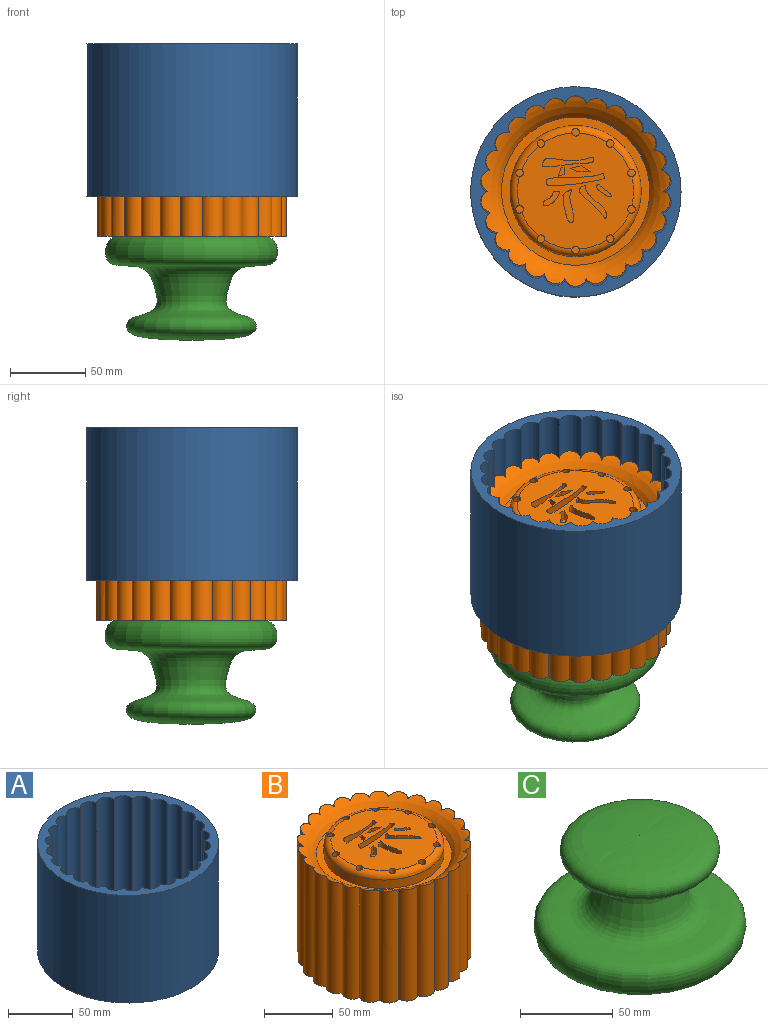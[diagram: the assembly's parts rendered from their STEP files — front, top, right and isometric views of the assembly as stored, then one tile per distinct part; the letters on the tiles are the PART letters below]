
ASSEMBLY  parts=3 mates=2
PART A: 30 faces, bbox 139.7x139.7x101.6 mm
  f0: plane 139.7x139.7mm, normal (0,0,-1), area 15327.9mm2, adj f1
  f1: cylinder r=69.85mm len=139.7mm, axis (0,0,-1), area 44590.3mm2, adj f0,f2
  f2: plane 139.7x139.7mm, normal (0,0,1), area 3055.9mm2, adj f1,f3,f4,f5,f6,f7,f8,f9
  f3: cylinder r=7.62mm len=99.06mm, axis (0,0,1), area 1835.1mm2, adj f2,f4,f11,f29
  f4: cylinder r=7.62mm len=99.06mm, axis (0,0,1), area 1835.1mm2, adj f2,f3,f28,f29
  f5: cylinder r=7.62mm len=99.06mm, axis (0,0,1), area 1835.1mm2, adj f2,f7,f10,f29
  f6: cylinder r=7.62mm len=99.06mm, axis (0,0,1), area 1835.1mm2, adj f2,f8,f9,f29
  f7: cylinder r=7.62mm len=99.06mm, axis (0,0,1), area 1835.1mm2, adj f2,f5,f8,f29
  f8: cylinder r=7.62mm len=99.06mm, axis (0,0,1), area 1835.1mm2, adj f2,f6,f7,f29
  f9: cylinder r=7.62mm len=99.06mm, axis (0,0,1), area 1835.1mm2, adj f2,f6,f12,f29
  f10: cylinder r=7.62mm len=99.06mm, axis (0,0,1), area 1835.1mm2, adj f2,f5,f11,f29
  f11: cylinder r=7.62mm len=99.06mm, axis (0,0,1), area 1835.1mm2, adj f2,f3,f10,f29
  f12: cylinder r=7.62mm len=99.06mm, axis (0,0,1), area 1835.1mm2, adj f2,f9,f13,f29
  f13: cylinder r=7.62mm len=99.06mm, axis (0,0,1), area 1835.1mm2, adj f2,f12,f14,f29
  f14: cylinder r=7.62mm len=99.06mm, axis (0,0,1), area 1835.1mm2, adj f2,f13,f15,f29
  f15: cylinder r=7.62mm len=99.06mm, axis (0,0,1), area 1835.1mm2, adj f2,f14,f16,f29
  f16: cylinder r=7.62mm len=99.06mm, axis (0,0,1), area 1835.1mm2, adj f2,f15,f17,f29
  f17: cylinder r=7.62mm len=99.06mm, axis (0,0,1), area 1835.1mm2, adj f2,f16,f18,f29
  f18: cylinder r=7.62mm len=99.06mm, axis (0,0,1), area 1835.1mm2, adj f2,f17,f19,f29
  f19: cylinder r=7.62mm len=99.06mm, axis (0,0,1), area 1835.1mm2, adj f2,f18,f20,f29
  f20: cylinder r=7.62mm len=99.06mm, axis (0,0,1), area 1835.1mm2, adj f2,f19,f21,f29
  f21: cylinder r=7.62mm len=99.06mm, axis (0,0,1), area 1835.1mm2, adj f2,f20,f22,f29
  f22: cylinder r=7.62mm len=99.06mm, axis (0,0,1), area 1835.1mm2, adj f2,f21,f23,f29
  f23: cylinder r=7.62mm len=99.06mm, axis (0,0,1), area 1835.1mm2, adj f2,f22,f24,f29
  f24: cylinder r=7.62mm len=99.06mm, axis (0,0,1), area 1835.1mm2, adj f2,f23,f25,f29
  f25: cylinder r=7.62mm len=99.06mm, axis (0,0,1), area 1835.1mm2, adj f2,f24,f27,f29
  f26: cylinder r=7.62mm len=99.06mm, axis (0,0,1), area 1835.1mm2, adj f2,f27,f28,f29
  f27: cylinder r=7.62mm len=99.06mm, axis (0,0,1), area 1835.1mm2, adj f2,f25,f26,f29
  f28: cylinder r=7.62mm len=99.06mm, axis (0,0,1), area 1835.1mm2, adj f2,f4,f26,f29
  f29: plane 127.62x126.8mm, normal (0,0,1), area 12272mm2, adj f3,f4,f5,f6,f7,f8,f9,f10
PART B: 77 faces, bbox 153.7x153.7x100.6 mm
  f0: plane 77.12x76.96mm, normal (0,0,1), area 4000.1mm2, adj f1,f32,f34,f36,f38,f40,f42,f44
  f1: torus R=38.56mm, axis (0,0,1), area 1934.2mm2, adj f0,f31,f32,f34,f36,f38,f40,f42
  f2: cylinder r=7.54mm len=99.33mm, axis (0,0,-1), area 1810.4mm2, adj f3,f4,f5,f30
  f3: plane 126.34x125.53mm, normal (0,0,-1), area 12027.8mm2, adj f2,f4,f5,f6,f7,f8,f9,f10
  f4: cylinder r=7.54mm len=99.33mm, axis (0,0,-1), area 1810.4mm2, adj f2,f3,f6,f30
  f5: cylinder r=7.54mm len=99.33mm, axis (0,0,-1), area 1810.4mm2, adj f2,f3,f12,f30
  f6: cylinder r=7.54mm len=99.33mm, axis (0,0,-1), area 1810.4mm2, adj f3,f4,f7,f30
  f7: cylinder r=7.54mm len=99.33mm, axis (0,0,-1), area 1810.4mm2, adj f3,f6,f8,f30
  f8: cylinder r=7.54mm len=99.33mm, axis (0,0,-1), area 1810.4mm2, adj f3,f7,f9,f30
  f9: cylinder r=7.54mm len=99.33mm, axis (0,0,-1), area 1810.4mm2, adj f3,f8,f10,f30
  f10: cylinder r=7.54mm len=99.33mm, axis (0,0,-1), area 1810.4mm2, adj f3,f9,f11,f30
  f11: cylinder r=7.54mm len=99.33mm, axis (0,0,-1), area 1810.4mm2, adj f3,f10,f28,f30
  f12: cylinder r=7.54mm len=99.33mm, axis (0,0,-1), area 1810.4mm2, adj f3,f5,f13,f30
  f13: cylinder r=7.54mm len=99.33mm, axis (0,0,-1), area 1810.4mm2, adj f3,f12,f14,f30
  f14: cylinder r=7.54mm len=99.33mm, axis (0,0,-1), area 1810.4mm2, adj f3,f13,f15,f30
  f15: cylinder r=7.54mm len=99.33mm, axis (0,0,-1), area 1810.4mm2, adj f3,f14,f16,f30
  f16: cylinder r=7.54mm len=99.33mm, axis (0,0,-1), area 1810.4mm2, adj f3,f15,f17,f30
  f17: cylinder r=7.54mm len=99.33mm, axis (0,0,-1), area 1810.4mm2, adj f3,f16,f18,f30
  f18: cylinder r=7.54mm len=99.33mm, axis (0,0,-1), area 1810.4mm2, adj f3,f17,f19,f30
  f19: cylinder r=7.54mm len=99.33mm, axis (0,0,-1), area 1810.4mm2, adj f3,f18,f20,f30
  f20: cylinder r=7.54mm len=99.33mm, axis (0,0,-1), area 1810.4mm2, adj f3,f19,f21,f30
  f21: cylinder r=7.54mm len=99.33mm, axis (0,0,-1), area 1810.4mm2, adj f3,f20,f22,f30
  f22: cylinder r=7.54mm len=99.33mm, axis (0,0,-1), area 1810.4mm2, adj f3,f21,f23,f30
  f23: cylinder r=7.54mm len=99.33mm, axis (0,0,-1), area 1810.4mm2, adj f3,f22,f24,f30
  f24: cylinder r=7.54mm len=99.33mm, axis (0,0,-1), area 1810.4mm2, adj f3,f23,f25,f30
  f25: cylinder r=7.54mm len=99.33mm, axis (0,0,-1), area 1810.4mm2, adj f3,f24,f26,f30
  f26: cylinder r=7.54mm len=99.33mm, axis (0,0,-1), area 1810.4mm2, adj f3,f25,f27,f30
  f27: cylinder r=7.54mm len=99.33mm, axis (0,0,-1), area 1810.4mm2, adj f3,f26,f28,f30
  f28: cylinder r=7.54mm len=99.33mm, axis (0,0,-1), area 1810.4mm2, adj f3,f11,f27,f30
  f29: plane 98.49x98.49mm, normal (0,0,1), area 1648.6mm2, adj f30,f31
  f30: torus R=71.02mm, axis (0,0,1), area 5854.1mm2, adj f2,f4,f5,f6,f7,f8,f9,f10
  f31: cylinder r=43.59mm len=87.18mm, axis (0,0,-1), area 2066.2mm2, adj f1,f29
  f32: cylinder r=2.55mm len=7.54mm, axis (0,0,1), area 116.3mm2, adj f0,f1,f33
  f33: plane 5.11x5.11mm, normal (0,0,1), area 20.5mm2, adj f32
  f34: cylinder r=2.55mm len=7.54mm, axis (0,0,1), area 116.3mm2, adj f0,f1,f35
  f35: plane 5.11x5.11mm, normal (0,0,1), area 20.5mm2, adj f34
  f36: cylinder r=2.55mm len=7.54mm, axis (0,0,1), area 116.3mm2, adj f0,f1,f37
  f37: plane 5.11x5.11mm, normal (0,0,1), area 20.5mm2, adj f36
  f38: cylinder r=2.55mm len=7.54mm, axis (0,0,1), area 116.3mm2, adj f0,f1,f39
  f39: plane 5.11x5.11mm, normal (0,0,1), area 20.5mm2, adj f38
  f40: cylinder r=2.55mm len=7.54mm, axis (0,0,1), area 116.3mm2, adj f0,f1,f41
  f41: plane 5.11x5.11mm, normal (0,0,1), area 20.5mm2, adj f40
  f42: cylinder r=2.55mm len=7.54mm, axis (0,0,1), area 116.3mm2, adj f0,f1,f43
  f43: plane 5.11x5.11mm, normal (0,0,1), area 20.5mm2, adj f42
  f44: cylinder r=2.55mm len=7.54mm, axis (0,0,1), area 116.3mm2, adj f0,f1,f45
  f45: plane 5.11x5.11mm, normal (0,0,1), area 20.5mm2, adj f44
  f46: cylinder r=2.55mm len=7.54mm, axis (0,0,1), area 116.3mm2, adj f0,f1,f47
  f47: plane 5.11x5.11mm, normal (0,0,1), area 20.5mm2, adj f46
  f48: cylinder r=2.55mm len=7.54mm, axis (0,0,1), area 116.3mm2, adj f0,f1,f49
  f49: plane 5.11x5.11mm, normal (0,0,1), area 20.5mm2, adj f48
  f50: cylinder r=2.55mm len=7.54mm, axis (0,0,1), area 116.3mm2, adj f0,f1,f51
  f51: plane 5.11x5.11mm, normal (0,0,1), area 20.5mm2, adj f50
  f52: extruded ~32.28x7.54mm, area 274.2mm2, adj f0,f53,f54
  f53: extruded ~34.1x7.54mm, area 290.2mm2, adj f0,f52,f54
  f54: plane 34.34x6.81mm, normal (0,0,1), area 118.8mm2, adj f52,f53
  f55: plane 7.54x2.26mm, normal (0.23,-0.97,0), area 17.5mm2, adj f0,f56,f58,f59
  f56: plane 7.54x5.33mm, normal (0.96,-0.29,0), area 42mm2, adj f0,f55,f57,f59
  f57: plane 7.54x3.84mm, normal (-0.23,0.97,0), area 29.8mm2, adj f0,f56,f58,f59
  f58: plane 7.54x4.96mm, normal (-1,0,0), area 37.4mm2, adj f0,f55,f57,f59
  f59: plane 5.86x3.84mm, normal (0,0,1), area 15.1mm2, adj f55,f56,f57,f58
  f60: plane 7.54x2.88mm, normal (0.63,-0.78,0), area 28mm2, adj f0,f61,f62
  f61: extruded ~21.76x7.54mm, area 345.1mm2, adj f0,f60,f62
  f62: plane 23.1x7.83mm, normal (0,0,1), area 94.2mm2, adj f60,f61
  f63: plane 7.54x4.08mm, normal (0,-1,0), area 30.8mm2, adj f0,f64,f65
  f64: extruded ~10.9x9.85mm, area 212.8mm2, adj f0,f63,f65
  f65: plane 11.17x10.13mm, normal (0,0,1), area 47.2mm2, adj f63,f64
  f66: plane 7.54x6.97mm, normal (0.23,-0.97,0), area 54mm2, adj f0,f67,f69,f70
  f67: plane 7.54x5.51mm, normal (0.4,0.92,0), area 45.4mm2, adj f0,f66,f68,f70
  f68: plane 7.96x7.54mm, normal (0,1,0), area 60.1mm2, adj f0,f67,f69,f70
  f69: plane 7.54x6.51mm, normal (-0.53,-0.85,0), area 57.8mm2, adj f0,f66,f68,f70
  f70: plane 13.47x4.05mm, normal (0,0,1), area 29mm2, adj f66,f67,f68,f69
  f71: extruded ~21.92x18.23mm, area 449mm2, adj f0,f72
  f72: plane 22.77x19.32mm, normal (0,0,1), area 92.2mm2, adj f71
  f73: extruded ~9.77x8.2mm, area 200.4mm2, adj f0,f74
  f74: plane 10.58x8.76mm, normal (0,0,1), area 30.4mm2, adj f73
  f75: extruded ~38.84x8.1mm, area 633.1mm2, adj f0,f76
  f76: plane 40.81x11.74mm, normal (0,0,1), area 171mm2, adj f75
PART C: 2 faces, bbox 114.5x114.5x69 mm
  f0: plane 101.6x101.6mm, normal (0,0,-1), area 8107.3mm2, adj f1
  f1: revolved ~114.51x114.51mm, area 30123.2mm2, adj f0
PLACE A t=(-14.29,20.07,-8.14)mm
PLACE B t=(-14.5,20.63,-34.63)mm
PLACE C rot(axis=(1,0,0),180deg) t=(-14.5,20.63,-34.63)mm
MATE fastened C.f0 <-> B.f30  axis (0,0,1) through (-14.5,20.63,-34.63)mm
MATE slider B.f0 <-> A.f1  axis (0,0,1) through (-14.29,20.07,65.95)mm
